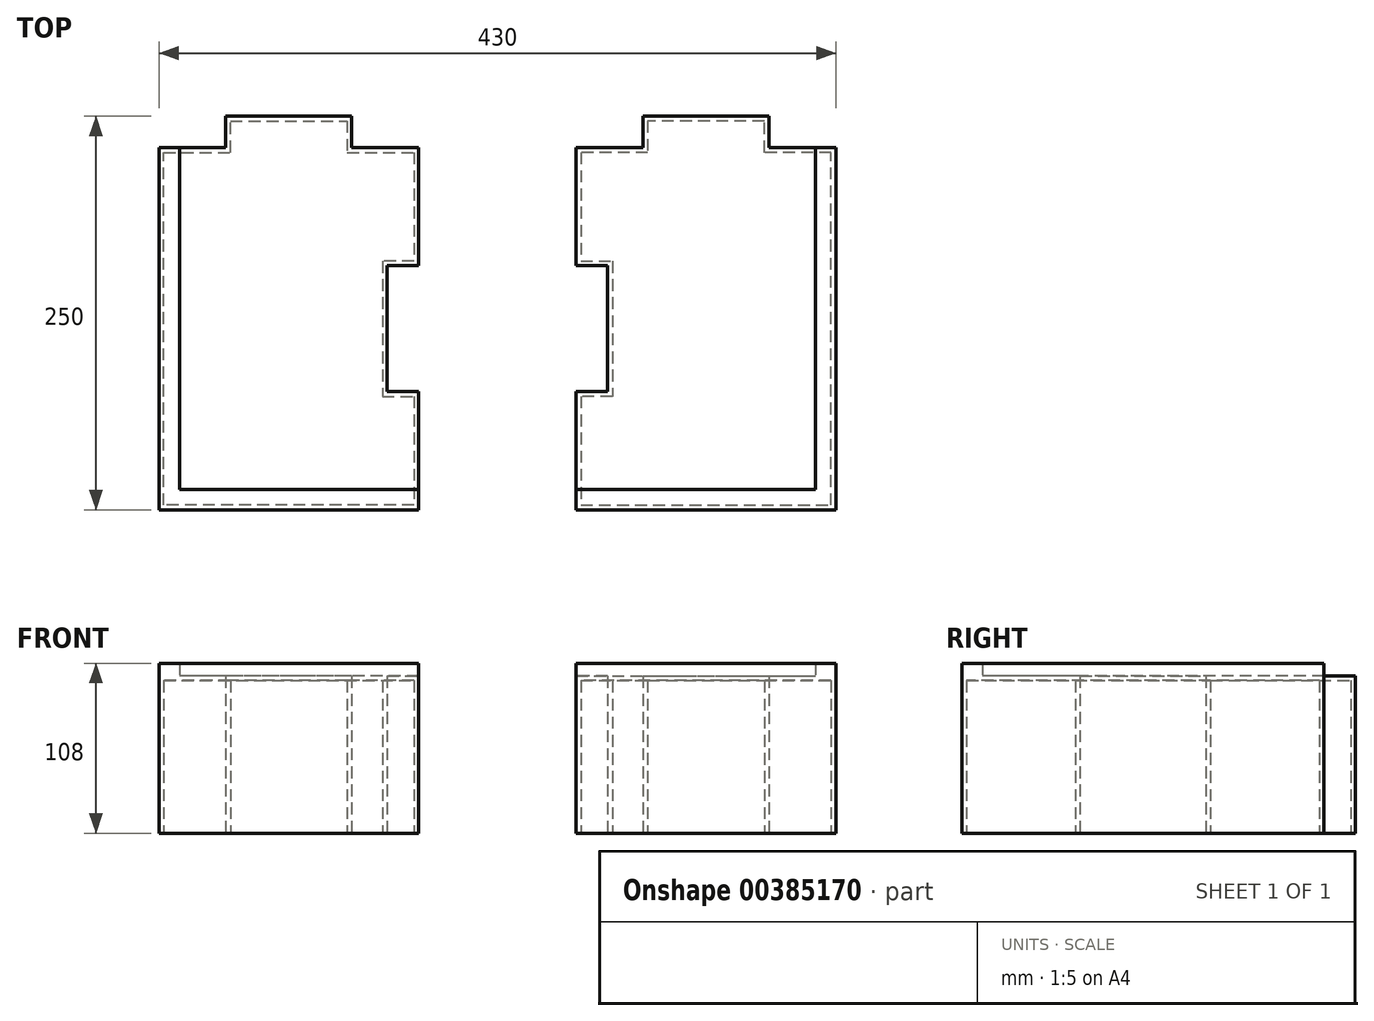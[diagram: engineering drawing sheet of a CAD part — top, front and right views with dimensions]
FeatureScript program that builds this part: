
annotation { "Feature Type Name" : "Feature", "Feature Type Description" : "" }
export const myFeature = defineFeature(function(context is Context, id is Id, definition is map)
    precondition{}
    {
        {
            var Q0;
            Q0=qCreatedBy(makeId("Top.planeOp"),FACE);
            var sketch = newSketch(context, id + "F0", { "sketchPlane" : qUnion([Q0])});
            skLineSegment(sketch, "E0.bottom", {"start": v(165, -230) * mm, "end": v(-165, -230) * mm});
            skLineSegment(sketch, "E0.top", {"start": v(165, 230) * mm, "end": v(-165, 230) * mm});
            skLineSegment(sketch, "E0.left", {"start": v(165, -230) * mm, "end": v(165, 230) * mm});
            skLineSegment(sketch, "E0.right", {"start": v(-165, -230) * mm, "end": v(-165, 230) * mm});
            skPoint(sketch, "E0.middle", {"position": v(0, 0) * mm});
            skLineSegment(sketch, "E1", {"start": v(165, 0) * mm, "end": v(122.5, 0) * mm});
            skLineSegment(sketch, "E2", {"start": v(0, -230) * mm, "end": v(0, -155) * mm});
            skLineSegment(sketch, "E3.bottom", {"start": v(0, -230) * mm, "end": v(165, -230) * mm});
            skLineSegment(sketch, "E3.top", {"start": v(0, 0) * mm, "end": v(42.5, 0) * mm});
            skLineSegment(sketch, "E3.right", {"start": v(165, -230) * mm, "end": v(165, 0) * mm});
            skLineSegment(sketch, "E4.top", {"start": v(165, 230) * mm, "end": v(0, 230) * mm});
            skLineSegment(sketch, "E4.left", {"start": v(165, 0) * mm, "end": v(165, 230) * mm});
            skLineSegment(sketch, "E4.right", {"start": v(0, 0) * mm, "end": v(0, 75) * mm});
            skLineSegment(sketch, "E5.bottom", {"start": v(0, 230) * mm, "end": v(-165, 230) * mm});
            skLineSegment(sketch, "E5.top", {"start": v(0, 0) * mm, "end": v(-42.5, 0) * mm});
            skLineSegment(sketch, "E5.left", {"start": v(0, 230) * mm, "end": v(0, 155) * mm});
            skLineSegment(sketch, "E5.right", {"start": v(-165, 230) * mm, "end": v(-165, 0) * mm});
            skLineSegment(sketch, "E6.bottom", {"start": v(-165, 0) * mm, "end": v(-122.5, 0) * mm});
            skLineSegment(sketch, "E6.top", {"start": v(-165, -230) * mm, "end": v(0, -230) * mm});
            skLineSegment(sketch, "E6.left", {"start": v(-165, 0) * mm, "end": v(-165, -230) * mm});
            skLineSegment(sketch, "E6.right", {"start": v(0, 0) * mm, "end": v(0, -75) * mm});
            skLineSegment(sketch, "E7.bottom", {"start": v(122.5, -20) * mm, "end": v(42.5, -20) * mm});
            skLineSegment(sketch, "E7.left", {"start": v(122.5, -20) * mm, "end": v(122.5, 0) * mm});
            skLineSegment(sketch, "E7.right", {"start": v(42.5, -20) * mm, "end": v(42.5, 0) * mm});
            skPoint(sketch, "E7.middle", {"position": v(82.5, 0) * mm});
            skPoint(sketch, "E7.top.end.orphan", {"position": v(42.5, 20) * mm});
            skPoint(sketch, "E8.orphan", {"position": v(122.5, 20) * mm});
            skLineSegment(sketch, "E9.bottom", {"start": v(-122.5, 20) * mm, "end": v(-42.5, 20) * mm});
            skLineSegment(sketch, "E9.left", {"start": v(-122.5, 20) * mm, "end": v(-122.5, 0) * mm});
            skLineSegment(sketch, "E9.right", {"start": v(-42.5, 20) * mm, "end": v(-42.5, 0) * mm});
            skPoint(sketch, "E9.middle", {"position": v(-82.5, 0) * mm});
            skPoint(sketch, "E9.top.start.orphan", {"position": v(-122.5, -20) * mm});
            skPoint(sketch, "E10.orphan", {"position": v(-42.5, -20) * mm});
            skLineSegment(sketch, "E11.bottom", {"start": v(20, 75) * mm, "end": v(0, 75) * mm});
            skLineSegment(sketch, "E11.top", {"start": v(20, 155) * mm, "end": v(0, 155) * mm});
            skLineSegment(sketch, "E11.left", {"start": v(20, 75) * mm, "end": v(20, 155) * mm});
            skPoint(sketch, "E11.middle", {"position": v(0, 115) * mm});
            skLineSegment(sketch, "E12.bottom", {"start": v(0, -155) * mm, "end": v(-20, -155) * mm});
            skLineSegment(sketch, "E12.top", {"start": v(0, -75) * mm, "end": v(-20, -75) * mm});
            skLineSegment(sketch, "E12.right", {"start": v(-20, -155) * mm, "end": v(-20, -75) * mm});
            skPoint(sketch, "E12.middle", {"position": v(0, -115) * mm});
            skPoint(sketch, "E11.right.end.orphan", {"position": v(-20, 155) * mm});
            skPoint(sketch, "E13.orphan", {"position": v(-20, 75) * mm});
            skPoint(sketch, "E12.left.end.orphan", {"position": v(20, -75) * mm});
            skPoint(sketch, "E14.orphan", {"position": v(20, -155) * mm});
            skLineSegment(sketch, "E15.trimOffspring", {"start": v(0, -155) * mm, "end": v(0, -230) * mm});
            skLineSegment(sketch, "E16.trimOffspring", {"start": v(0, -75) * mm, "end": v(0, 0) * mm});
            skLineSegment(sketch, "E17.trimOffspring", {"start": v(0, -75) * mm, "end": v(0, 75) * mm});
            skLineSegment(sketch, "E18.trimOffspring", {"start": v(42.5, 0) * mm, "end": v(0, 0) * mm});
            skLineSegment(sketch, "E19.trimOffspring", {"start": v(122.5, 0) * mm, "end": v(165, 0) * mm});
            skLineSegment(sketch, "E20.trimOffspring", {"start": v(42.5, 0) * mm, "end": v(-42.5, 0) * mm});
            skLineSegment(sketch, "E21.trimOffspring", {"start": v(0, 75) * mm, "end": v(0, 0) * mm});
            skLineSegment(sketch, "E22.trimOffspring", {"start": v(0, 155) * mm, "end": v(0, 230) * mm});
            skLineSegment(sketch, "E23.trimOffspring", {"start": v(-42.5, 0) * mm, "end": v(0, 0) * mm});
            skLineSegment(sketch, "E24.trimOffspring", {"start": v(-122.5, 0) * mm, "end": v(-165, 0) * mm});
            skSolve(sketch);
        }
        {
            var Q0;
            Q0=qCreatedBy(makeId("Top.planeOp"),FACE);
            var sketch = newSketch(context, id + "F1", { "sketchPlane" : qUnion([Q0])});
            skLineSegment(sketch, "E25.bottom", {"start": v(0, 0) * mm, "end": v(-42.5, 0) * mm});
            skLineSegment(sketch, "E25.top", {"start": v(0, -230) * mm, "end": v(-165, -230) * mm});
            skLineSegment(sketch, "E25.left", {"start": v(0, 0) * mm, "end": v(0, -75) * mm});
            skLineSegment(sketch, "E25.right", {"start": v(-165, 0) * mm, "end": v(-165, -230) * mm});
            skLineSegment(sketch, "E26.bottom", {"start": v(-42.5, 20) * mm, "end": v(-122.5, 20) * mm});
            skLineSegment(sketch, "E26.left", {"start": v(-42.5, 20) * mm, "end": v(-42.5, 0) * mm});
            skLineSegment(sketch, "E26.right", {"start": v(-122.5, 20) * mm, "end": v(-122.5, 0) * mm});
            skPoint(sketch, "E26.middle", {"position": v(-82.5, 0) * mm});
            skLineSegment(sketch, "E27.bottom", {"start": v(-20, -155) * mm, "end": v(0, -155) * mm});
            skLineSegment(sketch, "E27.top", {"start": v(-20, -75) * mm, "end": v(0, -75) * mm});
            skLineSegment(sketch, "E27.left", {"start": v(-20, -155) * mm, "end": v(-20, -75) * mm});
            skPoint(sketch, "E27.middle", {"position": v(0, -115) * mm});
            skPoint(sketch, "E27.right.end.orphan", {"position": v(20, -75) * mm});
            skPoint(sketch, "E28.orphan", {"position": v(20, -155) * mm});
            skLineSegment(sketch, "E29.trimOffspring", {"start": v(0, -155) * mm, "end": v(0, -230) * mm});
            skPoint(sketch, "E26.top.end.orphan", {"position": v(-122.5, -20) * mm});
            skPoint(sketch, "E30.orphan", {"position": v(-42.5, -20) * mm});
            skLineSegment(sketch, "E31.trimOffspring", {"start": v(-122.5, 0) * mm, "end": v(-165, 0) * mm});
            skLineSegment(sketch, "E32.0", {"start": v(-120.45, -2.05) * mm, "end": v(-162.95, -2.05) * mm});
            skLineSegment(sketch, "E32.1", {"start": v(-22.05, -157.05) * mm, "end": v(-22.05, -72.95) * mm});
            skLineSegment(sketch, "E32.2", {"start": v(-22.05, -157.05) * mm, "end": v(-2.05, -157.05) * mm});
            skLineSegment(sketch, "E32.3", {"start": v(-2.05, -157.05) * mm, "end": v(-2.05, -227.95) * mm});
            skLineSegment(sketch, "E32.4", {"start": v(-2.05, -227.95) * mm, "end": v(-162.95, -227.95) * mm});
            skLineSegment(sketch, "E32.5", {"start": v(-22.05, -72.95) * mm, "end": v(-2.05, -72.95) * mm});
            skLineSegment(sketch, "E32.6", {"start": v(-162.95, -2.05) * mm, "end": v(-162.95, -227.95) * mm});
            skLineSegment(sketch, "E32.7", {"start": v(-2.05, -2.05) * mm, "end": v(-2.05, -72.95) * mm});
            skLineSegment(sketch, "E32.8", {"start": v(-2.05, -2.05) * mm, "end": v(-44.55, -2.05) * mm});
            skLineSegment(sketch, "E32.9", {"start": v(-44.55, 17.95) * mm, "end": v(-44.55, -2.05) * mm});
            skLineSegment(sketch, "E32.10", {"start": v(-44.55, 17.95) * mm, "end": v(-120.45, 17.95) * mm});
            skLineSegment(sketch, "E32.11", {"start": v(-120.45, 17.95) * mm, "end": v(-120.45, -2.05) * mm});
            skSolve(sketch);
        }
        {
            var Q0;
            Q0=makeQuery(id+"F1.imprint","IMPRINT",FACE,{"disambiguationData":[TD([[makeQuery(id+"F1.imprint","IMPRINT",EDGE,{"derivedFrom":sQuery(id+"F1.wireOp",EDGE,"E25.bottom")}),1.0]])]});
            extrude(context, id + "F2", {"entities" : qUnion([Q0]), "depth" : 100 * mm});
        }
        {
            var Q0;
            Q0=makeQuery(id+"F2.opExtrude","CAP_FACE",FACE,{"disambiguationData":[OSD([sQuery(id+"F1.wireOp",EDGE,"E25.bottom"),sQuery(id+"F1.wireOp",EDGE,"E25.top"),sQuery(id+"F1.wireOp",EDGE,"E25.left"),sQuery(id+"F1.wireOp",EDGE,"E25.right"),sQuery(id+"F1.wireOp",EDGE,"E26.bottom"),sQuery(id+"F1.wireOp",EDGE,"E26.left"),sQuery(id+"F1.wireOp",EDGE,"E26.right"),sQuery(id+"F1.wireOp",EDGE,"E27.bottom"),sQuery(id+"F1.wireOp",EDGE,"E27.top"),sQuery(id+"F1.wireOp",EDGE,"E27.left"),sQuery(id+"F1.wireOp",EDGE,"E29.trimOffspring"),sQuery(id+"F1.wireOp",EDGE,"E31.trimOffspring"),sQuery(id+"F1.wireOp",EDGE,"E32.0"),sQuery(id+"F1.wireOp",EDGE,"E32.1"),sQuery(id+"F1.wireOp",EDGE,"E32.2"),sQuery(id+"F1.wireOp",EDGE,"E32.3"),sQuery(id+"F1.wireOp",EDGE,"E32.4"),sQuery(id+"F1.wireOp",EDGE,"E32.5"),sQuery(id+"F1.wireOp",EDGE,"E32.6"),sQuery(id+"F1.wireOp",EDGE,"E32.7"),sQuery(id+"F1.wireOp",EDGE,"E32.8"),sQuery(id+"F1.wireOp",EDGE,"E32.9"),sQuery(id+"F1.wireOp",EDGE,"E32.10"),sQuery(id+"F1.wireOp",EDGE,"E32.11")])],"isStart":false});
            var sketch = newSketch(context, id + "F3", { "sketchPlane" : qUnion([Q0])});
            skLineSegment(sketch, "E33", {"start": v(-165, -230) * mm, "end": v(0, -230) * mm});
            skLineSegment(sketch, "E34", {"start": v(0, -230) * mm, "end": v(0, -155) * mm});
            skLineSegment(sketch, "E35", {"start": v(0, -155) * mm, "end": v(-20, -155) * mm});
            skLineSegment(sketch, "E36", {"start": v(-20, -155) * mm, "end": v(-20, -75) * mm});
            skLineSegment(sketch, "E37", {"start": v(-20, -75) * mm, "end": v(0, -75) * mm});
            skLineSegment(sketch, "E38", {"start": v(0, -75) * mm, "end": v(0, 0) * mm});
            skLineSegment(sketch, "E39", {"start": v(0, 0) * mm, "end": v(-42.5, 0) * mm});
            skLineSegment(sketch, "E40", {"start": v(-42.5, 0) * mm, "end": v(-42.5, 20) * mm});
            skLineSegment(sketch, "E41", {"start": v(-42.5, 20) * mm, "end": v(-122.5, 20) * mm});
            skLineSegment(sketch, "E42", {"start": v(-122.5, 20) * mm, "end": v(-122.5, 0) * mm});
            skLineSegment(sketch, "E43", {"start": v(-122.5, 0) * mm, "end": v(-165, 0) * mm});
            skLineSegment(sketch, "E44", {"start": v(-165, 0) * mm, "end": v(-165, -230) * mm});
            skSolve(sketch);
        }
        {
            var Q0;
            Q0=qSketchRegion(id+"F3",true);
            extrude(context, id + "F4", {"entities" : qUnion([Q0]), "operationType" : NewBodyOperationType.ADD, "oppositeDirection" : true, "depth" : 3 * mm});
        }
        {
            var Q0;
            Q0=makeQuery(id+"F4.boolean.opBoolean","MERGE",FACE,{"derivedFrom":[makeQuery(id+"F2.opExtrude","CAP_FACE",FACE,{"disambiguationData":[OSD([sQuery(id+"F1.wireOp",EDGE,"E25.bottom"),sQuery(id+"F1.wireOp",EDGE,"E25.top"),sQuery(id+"F1.wireOp",EDGE,"E25.left"),sQuery(id+"F1.wireOp",EDGE,"E25.right"),sQuery(id+"F1.wireOp",EDGE,"E26.bottom"),sQuery(id+"F1.wireOp",EDGE,"E26.left"),sQuery(id+"F1.wireOp",EDGE,"E26.right"),sQuery(id+"F1.wireOp",EDGE,"E27.bottom"),sQuery(id+"F1.wireOp",EDGE,"E27.top"),sQuery(id+"F1.wireOp",EDGE,"E27.left"),sQuery(id+"F1.wireOp",EDGE,"E29.trimOffspring"),sQuery(id+"F1.wireOp",EDGE,"E31.trimOffspring"),sQuery(id+"F1.wireOp",EDGE,"E32.0"),sQuery(id+"F1.wireOp",EDGE,"E32.1"),sQuery(id+"F1.wireOp",EDGE,"E32.2"),sQuery(id+"F1.wireOp",EDGE,"E32.3"),sQuery(id+"F1.wireOp",EDGE,"E32.4"),sQuery(id+"F1.wireOp",EDGE,"E32.5"),sQuery(id+"F1.wireOp",EDGE,"E32.6"),sQuery(id+"F1.wireOp",EDGE,"E32.7"),sQuery(id+"F1.wireOp",EDGE,"E32.8"),sQuery(id+"F1.wireOp",EDGE,"E32.9"),sQuery(id+"F1.wireOp",EDGE,"E32.10"),sQuery(id+"F1.wireOp",EDGE,"E32.11")])],"isStart":false}),makeQuery(id+"F4.opExtrude","CAP_FACE",FACE,{"disambiguationData":[OSD([sQuery(id+"F3.wireOp",EDGE,"E33"),sQuery(id+"F3.wireOp",EDGE,"E34"),sQuery(id+"F3.wireOp",EDGE,"E35"),sQuery(id+"F3.wireOp",EDGE,"E36"),sQuery(id+"F3.wireOp",EDGE,"E37"),sQuery(id+"F3.wireOp",EDGE,"E38"),sQuery(id+"F3.wireOp",EDGE,"E39"),sQuery(id+"F3.wireOp",EDGE,"E40"),sQuery(id+"F3.wireOp",EDGE,"E41"),sQuery(id+"F3.wireOp",EDGE,"E42"),sQuery(id+"F3.wireOp",EDGE,"E43"),sQuery(id+"F3.wireOp",EDGE,"E44")])],"isStart":true})]});
            var sketch = newSketch(context, id + "F5", { "sketchPlane" : qUnion([Q0])});
            skLineSegment(sketch, "E45.bottom", {"start": v(0, -230) * mm, "end": v(-160, -230) * mm});
            skLineSegment(sketch, "E45.top", {"start": v(0, -217) * mm, "end": v(-152, -217) * mm});
            skLineSegment(sketch, "E45.left", {"start": v(0, -230) * mm, "end": v(0, -217) * mm});
            skLineSegment(sketch, "E46.bottom", {"start": v(-165, 0) * mm, "end": v(-152, 0) * mm});
            skLineSegment(sketch, "E46.top", {"start": v(-165, -230) * mm, "end": v(-152, -230) * mm});
            skLineSegment(sketch, "E46.left", {"start": v(-165, 0) * mm, "end": v(-165, -230) * mm});
            skLineSegment(sketch, "E46.right", {"start": v(-152, 0) * mm, "end": v(-152, -217) * mm});
            skSolve(sketch);
        }
        {
            var Q0;
            {var subQ0=sQuery(id+"F5.wireOp",EDGE,"E45.bottom");Q0=makeQuery(id+"F5.imprint","IMPRINT",FACE,{"disambiguationData":[TD([[makeQuery(id+"F5.imprint","IMPRINT",EDGE,{"derivedFrom":subQ0}),-1.0]])]});}
            extrude(context, id + "F6", {"entities" : qUnion([Q0]), "operationType" : NewBodyOperationType.ADD, "depth" : 8 * mm});
        }
        {
            var Q0;
            Q0=makeQuery(id+"F2.opExtrude","CAP_FACE",FACE,{"disambiguationData":[OSD([sQuery(id+"F1.wireOp",EDGE,"E25.bottom"),sQuery(id+"F1.wireOp",EDGE,"E25.top"),sQuery(id+"F1.wireOp",EDGE,"E25.left"),sQuery(id+"F1.wireOp",EDGE,"E25.right"),sQuery(id+"F1.wireOp",EDGE,"E26.bottom"),sQuery(id+"F1.wireOp",EDGE,"E26.left"),sQuery(id+"F1.wireOp",EDGE,"E26.right"),sQuery(id+"F1.wireOp",EDGE,"E27.bottom"),sQuery(id+"F1.wireOp",EDGE,"E27.top"),sQuery(id+"F1.wireOp",EDGE,"E27.left"),sQuery(id+"F1.wireOp",EDGE,"E29.trimOffspring"),sQuery(id+"F1.wireOp",EDGE,"E31.trimOffspring"),sQuery(id+"F1.wireOp",EDGE,"E32.0"),sQuery(id+"F1.wireOp",EDGE,"E32.1"),sQuery(id+"F1.wireOp",EDGE,"E32.2"),sQuery(id+"F1.wireOp",EDGE,"E32.3"),sQuery(id+"F1.wireOp",EDGE,"E32.4"),sQuery(id+"F1.wireOp",EDGE,"E32.5"),sQuery(id+"F1.wireOp",EDGE,"E32.6"),sQuery(id+"F1.wireOp",EDGE,"E32.7"),sQuery(id+"F1.wireOp",EDGE,"E32.8"),sQuery(id+"F1.wireOp",EDGE,"E32.9"),sQuery(id+"F1.wireOp",EDGE,"E32.10"),sQuery(id+"F1.wireOp",EDGE,"E32.11")])],"isStart":true});
            var sketch = newSketch(context, id + "F7", { "sketchPlane" : qUnion([Q0])});
            skLineSegment(sketch, "E47", {"start": v(-165, 0) * mm, "end": v(-122.5, 0) * mm});
            skLineSegment(sketch, "E48", {"start": v(-122.5, 0) * mm, "end": v(-122.5, -20) * mm});
            skLineSegment(sketch, "E49", {"start": v(-122.5, -20) * mm, "end": v(-42.5, -20) * mm});
            skLineSegment(sketch, "E50", {"start": v(-42.5, -20) * mm, "end": v(-42.5, 0) * mm});
            skLineSegment(sketch, "E51", {"start": v(-42.5, 0) * mm, "end": v(0, 0) * mm});
            skLineSegment(sketch, "E52", {"start": v(0, 0) * mm, "end": v(0, 75) * mm});
            skLineSegment(sketch, "E53", {"start": v(0, 75) * mm, "end": v(-20, 75) * mm});
            skLineSegment(sketch, "E54", {"start": v(-20, 75) * mm, "end": v(-20, 155) * mm});
            skLineSegment(sketch, "E55", {"start": v(-20, 155) * mm, "end": v(0, 155) * mm});
            skLineSegment(sketch, "E56", {"start": v(0, 155) * mm, "end": v(0, 230) * mm});
            skLineSegment(sketch, "E57", {"start": v(0, 230) * mm, "end": v(-165, 230) * mm});
            skLineSegment(sketch, "E58", {"start": v(-165, 230) * mm, "end": v(-165, 0) * mm});
            skLineSegment(sketch, "E59.0", {"start": v(-162, 227) * mm, "end": v(-162, 3) * mm});
            skLineSegment(sketch, "E59.1", {"start": v(-45.5, 3) * mm, "end": v(-3, 3) * mm});
            skLineSegment(sketch, "E59.2", {"start": v(-45.5, -17) * mm, "end": v(-45.5, 3) * mm});
            skLineSegment(sketch, "E59.3", {"start": v(-119.5, -17) * mm, "end": v(-45.5, -17) * mm});
            skLineSegment(sketch, "E59.4", {"start": v(-119.5, 3) * mm, "end": v(-119.5, -17) * mm});
            skLineSegment(sketch, "E59.5", {"start": v(-3, 3) * mm, "end": v(-3, 72) * mm});
            skLineSegment(sketch, "E59.6", {"start": v(-162, 3) * mm, "end": v(-119.5, 3) * mm});
            skLineSegment(sketch, "E59.7", {"start": v(-3, 72) * mm, "end": v(-23, 72) * mm});
            skLineSegment(sketch, "E59.8", {"start": v(-23, 72) * mm, "end": v(-23, 158) * mm});
            skLineSegment(sketch, "E59.9", {"start": v(-23, 158) * mm, "end": v(-3, 158) * mm});
            skLineSegment(sketch, "E59.10", {"start": v(-3, 158) * mm, "end": v(-3, 227) * mm});
            skLineSegment(sketch, "E59.11", {"start": v(-3, 227) * mm, "end": v(-162, 227) * mm});
            skSolve(sketch);
        }
        {
            var Q0;
            Q0=qCreatedBy(makeId("Right.planeOp"),FACE);
            cPlane(context, id + "F8", {"entities" : qUnion([Q0]), "cplaneType" : CPlaneType.OFFSET, "offset" : 50 * mm, "width" : 150 * mm, "height" : 150 * mm});
        }
        {
            var Q0;
            Q0 = qSketchRegion(id + "F7", true);
            extrude(context, id + "F9", {"entities" : qUnion([Q0]), "operationType" : NewBodyOperationType.ADD, "oppositeDirection" : true, "depth" : 100 * mm});
        }
        {
            var Q0;
            Q0=makeQuery(id+"F2.opExtrude","SWEPT_BODY",BODY,{"disambiguationData":[OSD([sQuery(id+"F1.wireOp",EDGE,"E25.bottom"),sQuery(id+"F1.wireOp",EDGE,"E25.top"),sQuery(id+"F1.wireOp",EDGE,"E25.left"),sQuery(id+"F1.wireOp",EDGE,"E25.right"),sQuery(id+"F1.wireOp",EDGE,"E26.bottom"),sQuery(id+"F1.wireOp",EDGE,"E26.left"),sQuery(id+"F1.wireOp",EDGE,"E26.right"),sQuery(id+"F1.wireOp",EDGE,"E27.bottom"),sQuery(id+"F1.wireOp",EDGE,"E27.top"),sQuery(id+"F1.wireOp",EDGE,"E27.left"),sQuery(id+"F1.wireOp",EDGE,"E29.trimOffspring"),sQuery(id+"F1.wireOp",EDGE,"E31.trimOffspring"),sQuery(id+"F1.wireOp",EDGE,"E32.0"),sQuery(id+"F1.wireOp",EDGE,"E32.1"),sQuery(id+"F1.wireOp",EDGE,"E32.2"),sQuery(id+"F1.wireOp",EDGE,"E32.3"),sQuery(id+"F1.wireOp",EDGE,"E32.4"),sQuery(id+"F1.wireOp",EDGE,"E32.5"),sQuery(id+"F1.wireOp",EDGE,"E32.6"),sQuery(id+"F1.wireOp",EDGE,"E32.7"),sQuery(id+"F1.wireOp",EDGE,"E32.8"),sQuery(id+"F1.wireOp",EDGE,"E32.9"),sQuery(id+"F1.wireOp",EDGE,"E32.10"),sQuery(id+"F1.wireOp",EDGE,"E32.11")])]});
            var Q1;
            Q1=qCreatedBy(id+"F8.planeOp",FACE);
            mirror(context, id + "F10", {"entities" : qUnion([Q0]), "mirrorPlane" : qUnion([Q1])});
        }
    });
